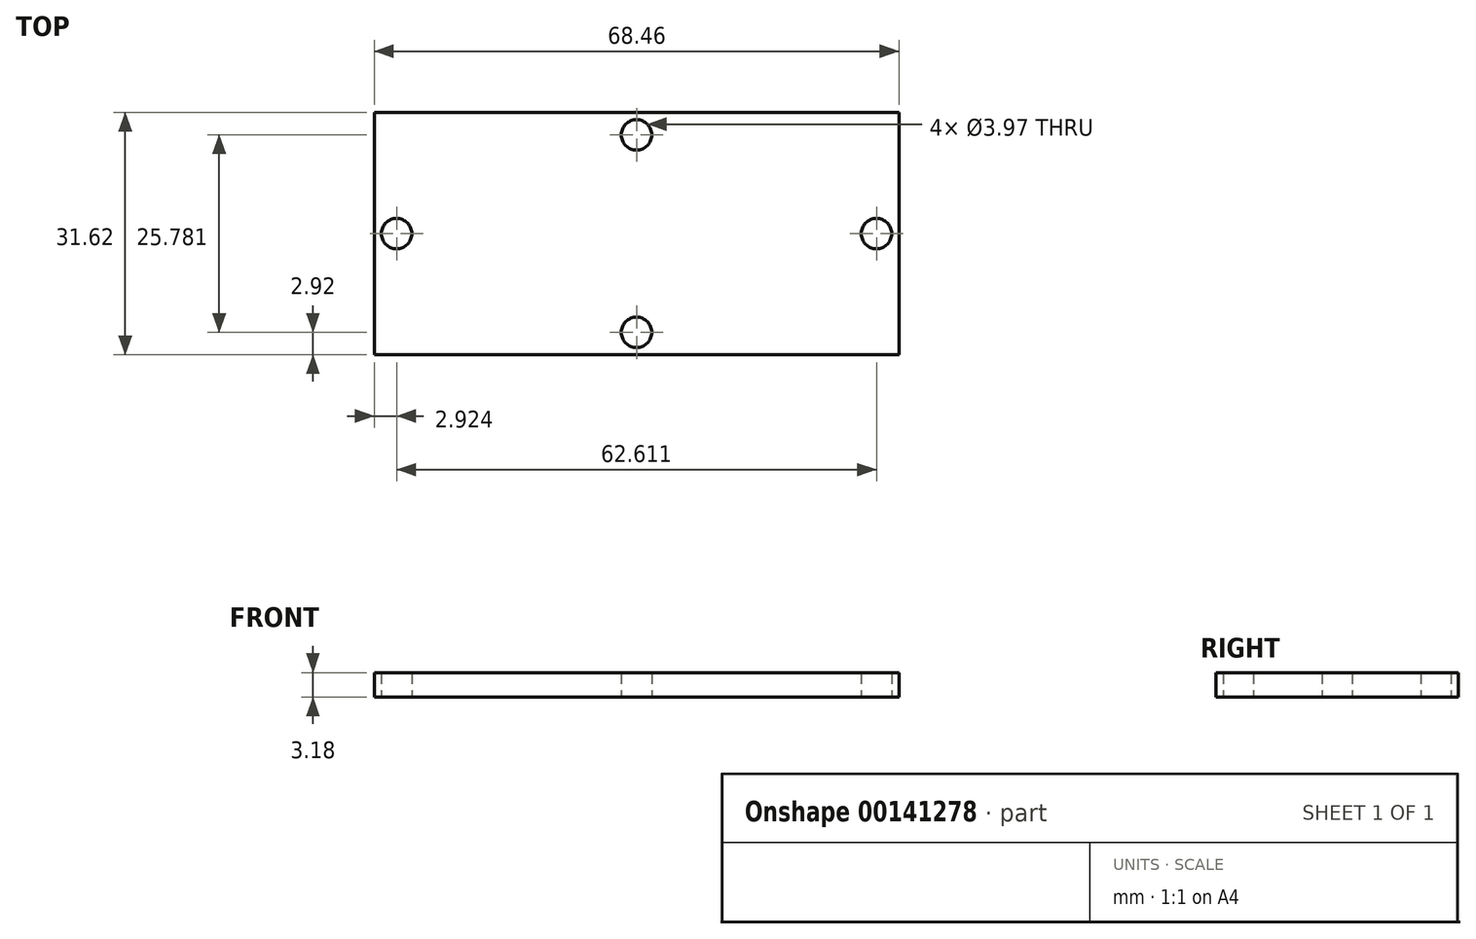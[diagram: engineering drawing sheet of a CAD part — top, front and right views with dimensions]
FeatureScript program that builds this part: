
annotation { "Feature Type Name" : "Feature", "Feature Type Description" : "" }
export const myFeature = defineFeature(function(context is Context, id is Id, definition is map)
    precondition{}
    {
        {
            var Q0;
            Q0=qCreatedBy(makeId("Top.planeOp"),FACE);
            var sketch = newSketch(context, id + "F0", { "sketchPlane" : qUnion([Q0])});
            skLineSegment(sketch, "E0.bottom", {"start": v(34.23, 15.81) * mm, "end": v(-34.23, 15.81) * mm});
            skLineSegment(sketch, "E0.top", {"start": v(34.23, -15.81) * mm, "end": v(-34.23, -15.81) * mm});
            skLineSegment(sketch, "E0.left", {"start": v(34.23, 15.81) * mm, "end": v(34.23, -15.81) * mm});
            skLineSegment(sketch, "E0.right", {"start": v(-34.23, 15.81) * mm, "end": v(-34.23, -15.81) * mm});
            skPoint(sketch, "E0.middle", {"position": v(0, 0) * mm});
            skCircle(sketch, "E1", {"center": v(0, 12.9) * mm, "radius": 1.98 * mm});
            skCircle(sketch, "E2", {"center": v(31.3, 0) * mm, "radius": 1.98 * mm});
            skCircle(sketch, "E3", {"center": v(0, -12.9) * mm, "radius": 1.98 * mm});
            skCircle(sketch, "E4", {"center": v(-31.3, 0) * mm, "radius": 1.98 * mm});
            skSolve(sketch);
        }
        {
            var Q0;
            Q0=makeQuery(id+"F0.imprint","IMPRINT",FACE,{"disambiguationData":[TD([[makeQuery(id+"F0.imprint","IMPRINT",EDGE,{"derivedFrom":sQuery(id+"F0.wireOp",EDGE,"E0.bottom")}),1.0]])]});
            extrude(context, id + "F1", {"entities" : qUnion([Q0]), "depth" : 3.17 * mm});
        }
    });
